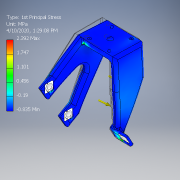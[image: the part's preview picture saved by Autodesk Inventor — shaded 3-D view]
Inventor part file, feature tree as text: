
AUTODESK INVENTOR PART (.ipt)
format: ipt  version: 2019.4 (Build 234330000, 330)  size: 545,280 bytes
history: native  units: mm
features: fillet x11, extrude x8, sketch x8
ambient origin geometry x8: Origin, YZ Plane, XZ Plane, XY Plane, X Axis, Y Axis, Z Axis, Center Point
bodies: Solid1 (feature_tree)
feature tree (27):
  extrude  "Extrusion1"  Depth=42.3mm
  extrude  "Extrusion2"  Depth=10.0mm
  sketch  "Sketch3"  dims[d5=42.3mm d6=15.0mm d7=0.0mm]
  extrude  "Extrusion4"  Depth=15.0mm TaperAngle=0.0deg
  extrude  "Extrusion10"  Depth=5.65mm
  fillet  "Fillet2"  Radius=3.5mm
  fillet  "Fillet3"  Radius=21.15mm
  fillet  "Fillet4"  Radius=8.0mm
  fillet  "Fillet5"  Radius=10.0mm
  fillet  "Fillet7"  Radius=12.2mm
  fillet  "Fillet8"  Radius=100.0mm
  extrude  "Extrusion12"  Depth=10.0mm
  extrude  "Extrusion13"  Depth=20.0mm
  extrude  "Extrusion14"  Depth=20.0mm
  fillet  "Fillet9"  Radius=30.0mm
  fillet  "Fillet10"  Radius=5.5mm
  fillet  "Fillet11"  Radius=20.0mm
  fillet  "Fillet12"  [1 undecoded]
  extrude  "Extrusion15"  Depth=20.0mm
  fillet  "Fillet13"  Radius=20.0mm
  sketch  "Sketch1"  dims[d0=52.3mm d1=42.3mm]
  sketch  "Sketch2"  dims[d2=7.0mm d3=0.0mm d4=10.0mm]
  sketch  "Sketch4"  dims[d8=5.65mm d9=5.65mm d10=3.5mm]
  sketch  "Sketch9"  dims[d11=20.0mm d13=31.0mm d14=20.0mm d16=31.0mm d21=21.15mm d22=8.0mm d23=10.0mm d24=0.0mm d77=12.2mm d78=100.0mm]
  sketch  "Sketch12"  dims[d79=60.0deg d80=10.0mm]
  sketch  "Sketch13"  dims[d81=90.0deg d82=20.0mm]
  sketch  "Sketch14"  dims[d83=60.0deg d84=20.0mm d85=30.0mm d88=5.5mm d90=20.0mm d91=60.0deg d92=20.0mm d103=20.0mm d105=60.0mm d106=10.0mm d108=10.0mm d110=10.0mm d111=0.0mm d112=10.0mm d113=2.0mm d114=4.0mm d115=4.0mm d117=4.0mm d118=2.0mm d131=29.994mm d132=60.0deg d133=9.995mm d134=1.0mm d135=30.0deg d136=19.99mm d137=120.0deg d138=5.0mm d139=42.3mm d140=40.0mm d141=10.0mm d142=0.0mm d143=15.0mm d144=0.0mm d145=8.0mm d146=5.1mm d147=5.0mm d148=0.0mm d149=4.0mm d150=4.0mm d151=4.0mm d152=4.0mm d153=1.5mm d155=10.0mm d156=1.5mm d157=3.5mm d158=20.0mm d160=34.0mm d161=20.0mm d163=34.0mm d166=15.0mm d167=0.0mm d168=2.0mm]
note: 1 required parameter value undecoded (feature->parameter linkage not recoverable at this tier; creation-order binding heuristic only, values carry confidence <= 0.55)
